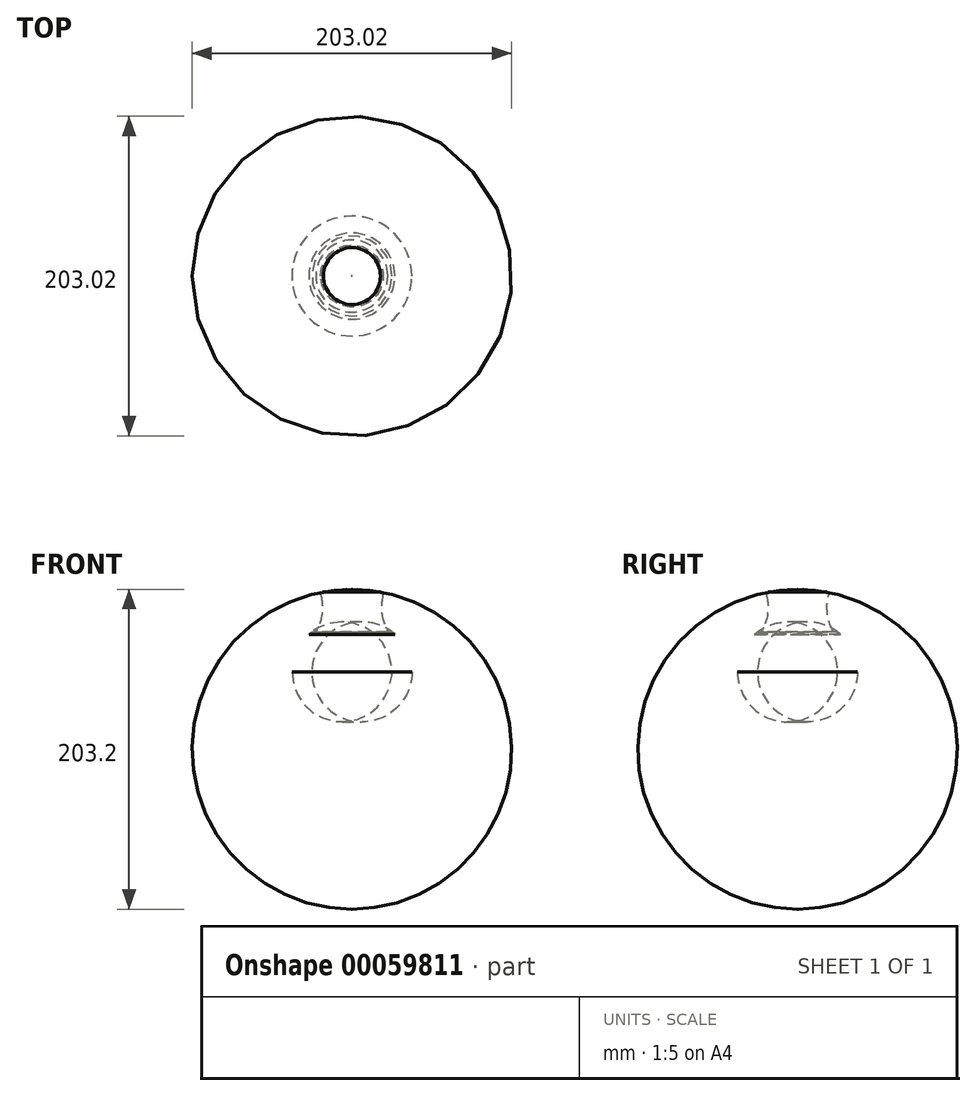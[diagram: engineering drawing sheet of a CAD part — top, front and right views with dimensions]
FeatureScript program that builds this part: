
annotation { "Feature Type Name" : "Feature", "Feature Type Description" : "" }
export const myFeature = defineFeature(function(context is Context, id is Id, definition is map)
    precondition{}
    {
        {
            var Q0;
            Q0=qCreatedBy(makeId("Front.planeOp"),FACE);
            var sketch = newSketch(context, id + "F0", { "sketchPlane" : qUnion([Q0])});
            skLineSegment(sketch, "E0", {"start": v(-23.15, 25.4) * mm, "end": v(0, 25.4) * mm});
            skArc(sketch, "E1", {"start": v(-27.35, 23.81) * mm, "mid": v(-35.29, 13.06) * mm, "end": v(-38.1, 0) * mm});
            skLineSegment(sketch, "E2", {"start": v(0, 0) * mm, "end": v(0, 25.4) * mm});
            skLineSegment(sketch, "E3", {"start": v(-38.1, 0) * mm, "end": v(0, 0) * mm});
            skPoint(sketch, "E4.visualSharp", {"position": v(-25.4, 25.4) * mm});
            skArc(sketch, "E4.filletArc", {"start": v(-23.15, 25.4) * mm, "mid": v(-25.4, 24.99) * mm, "end": v(-27.35, 23.81) * mm});
            skSolve(sketch);
        }
        {
            var Q0;
            Q0 = qSketchRegion(id + "F0", true);
            var Q1;
            Q1=sQuery(id+"F0.wireOp",EDGE,"E2");
            revolve(context, id + "F1", {"entities" : qUnion([Q0]), "axis" : qUnion([Q1]), "revolveType" : RevolveType.FULL});
        }
        {
            var Q0;
            Q0=qCreatedBy(makeId("Right.planeOp"),FACE);
            var sketch = newSketch(context, id + "F2", { "sketchPlane" : qUnion([Q0])});
            skLineSegment(sketch, "E5", {"start": v(0, 25.4) * mm, "end": v(-22.86, 25.4) * mm});
            skArc(sketch, "E6", {"start": v(-22.86, 25.4) * mm, "mid": v(-18.92, 37.83) * mm, "end": v(-20.32, 50.8) * mm});
            skLineSegment(sketch, "E7", {"start": v(-20.32, 50.8) * mm, "end": v(0, 50.8) * mm});
            skLineSegment(sketch, "E8", {"start": v(0, 50.8) * mm, "end": v(0, 25.4) * mm});
            skSolve(sketch);
        }
        {
            var Q0;
            Q0 = qSketchRegion(id + "F2", true);
            var Q1;
            Q1=sQuery(id+"F2.wireOp",EDGE,"E8");
            revolve(context, id + "F3", {"entities" : qUnion([Q0]), "axis" : qUnion([Q1]), "revolveType" : RevolveType.FULL});
        }
        {
            var Q0;
            Q0=makeQuery(id+"F3.opRevolve","SWEPT_EDGE",EDGE,{"disambiguationData":[OSD([sQuery(id+"F2.wireOp",EDGE,"E6"),sQuery(id+"F2.wireOp",EDGE,"E7")])]});
            fillet(context, id + "F4", {"entities" : qUnion([Q0]), "radius" : 1.27 * mm, "tangentPropagation" : true, "allowEdgeOverflow" : false});
        }
        {
            var Q0;
            Q0=qCreatedBy(makeId("Right.planeOp"),FACE);
            var sketch = newSketch(context, id + "F5", { "sketchPlane" : qUnion([Q0])});
            skLineSegment(sketch, "E9", {"start": v(-18.08, 50.8) * mm, "end": v(0, 50.8) * mm});
            skArc(sketch, "E10", {"start": v(0, 52.4) * mm, "mid": v(-9.07, 52) * mm, "end": v(-18.08, 50.8) * mm});
            skLineSegment(sketch, "E11", {"start": v(0, 52.4) * mm, "end": v(0, 50.8) * mm});
            skPoint(sketch, "E11.endSnap0", {"position": v(-0.1, 50.8) * mm});
            skPoint(sketch, "E12.orphan", {"position": v(17.9, 50.8) * mm});
            skSolve(sketch);
        }
        {
            var Q0;
            Q0=makeQuery(id+"F5.imprint","IMPRINT",FACE,{"disambiguationData":[TD([[makeQuery(id+"F5.imprint","IMPRINT",EDGE,{"derivedFrom":sQuery(id+"F5.wireOp",EDGE,"E9")}),1.0]])]});
            var Q1;
            Q1=sQuery(id+"F5.wireOp",EDGE,"E11");
            revolve(context, id + "F6", {"entities" : qUnion([Q0]), "axis" : qUnion([Q1]), "revolveType" : RevolveType.FULL});
        }
    });
